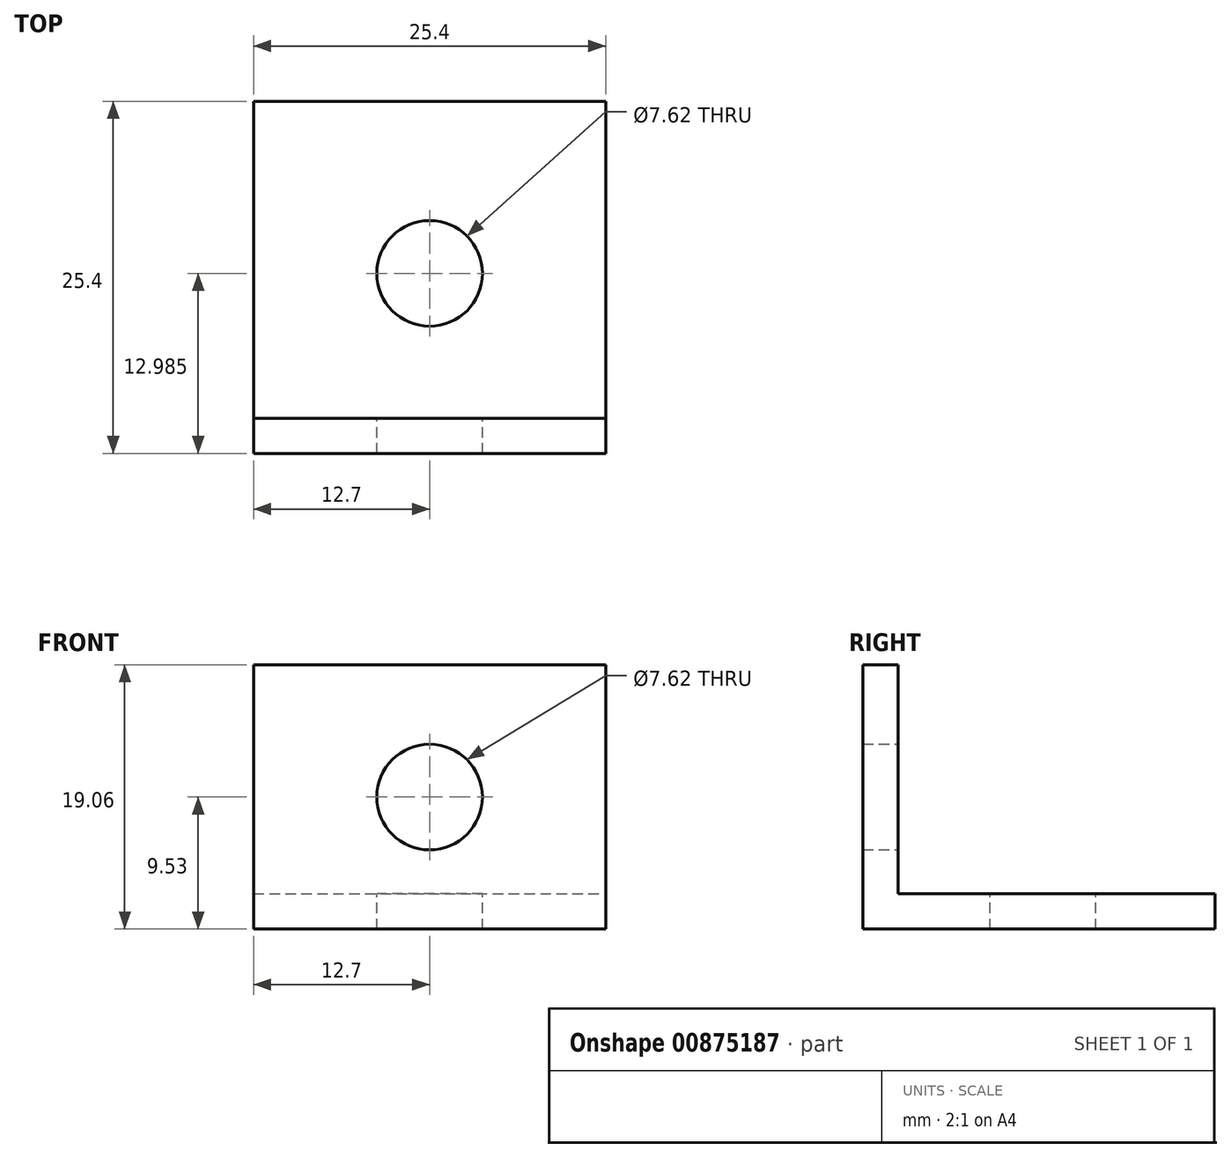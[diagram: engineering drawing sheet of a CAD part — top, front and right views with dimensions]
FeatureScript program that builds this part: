
annotation { "Feature Type Name" : "Feature", "Feature Type Description" : "" }
export const myFeature = defineFeature(function(context is Context, id is Id, definition is map)
    precondition{}
    {
        {
            var Q0;
            Q0=qCreatedBy(makeId("Front.planeOp"),FACE);
            var sketch = newSketch(context, id + "F0", { "sketchPlane" : qUnion([Q0])});
            skLineSegment(sketch, "E0.bottom", {"start": v(-12.7, 9.53) * mm, "end": v(12.7, 9.53) * mm});
            skLineSegment(sketch, "E0.top", {"start": v(-12.7, -9.52) * mm, "end": v(12.7, -9.52) * mm});
            skLineSegment(sketch, "E0.left", {"start": v(-12.7, 9.53) * mm, "end": v(-12.7, -9.52) * mm});
            skLineSegment(sketch, "E0.right", {"start": v(12.7, 9.53) * mm, "end": v(12.7, -9.52) * mm});
            skPoint(sketch, "E0.middle", {"position": v(0, 0) * mm});
            skSolve(sketch);
        }
        {
            var Q0;
            Q0=makeQuery(id+"F0.imprint","IMPRINT",FACE,{"disambiguationData":[TD([[makeQuery(id+"F0.imprint","IMPRINT",EDGE,{"derivedFrom":sQuery(id+"F0.wireOp",EDGE,"E0.bottom")}),-1.0]])]});
            extrude(context, id + "F1", {"entities" : qUnion([Q0]), "depth" : 25.4 * mm, "offsetDistance" : 25.4 * mm});
        }
        {
            var Q0;
            Q0=makeQuery(id+"F1.opExtrude","SWEPT_FACE",FACE,{"disambiguationData":[OSD([sQuery(id+"F0.wireOp",EDGE,"E0.right")])]});
            var Q1;
            Q1=makeQuery(id+"F1.opExtrude","SWEPT_FACE",FACE,{"disambiguationData":[OSD([sQuery(id+"F0.wireOp",EDGE,"E0.bottom")])]});
            var Q2;
            Q2=makeQuery(id+"F1.opExtrude","CAP_FACE",FACE,{"disambiguationData":[OSD([sQuery(id+"F0.wireOp",EDGE,"E0.bottom"),sQuery(id+"F0.wireOp",EDGE,"E0.top"),sQuery(id+"F0.wireOp",EDGE,"E0.left"),sQuery(id+"F0.wireOp",EDGE,"E0.right")])],"isStart":true});
            var Q3;
            Q3=makeQuery(id+"F1.opExtrude","SWEPT_FACE",FACE,{"disambiguationData":[OSD([sQuery(id+"F0.wireOp",EDGE,"E0.left")])]});
            shell(context, id + "F2", {"entities" : qUnion([Q0, Q1, Q2, Q3]), "thickness" : 2.54 * mm});
        }
        {
            var Q0;
            Q0=makeQuery(id+"F2.opShell","OFFSET_FACE",FACE,{"disambiguationData":[OSD([sQuery(id+"F0.wireOp",EDGE,"E0.bottom"),sQuery(id+"F0.wireOp",EDGE,"E0.top"),sQuery(id+"F0.wireOp",EDGE,"E0.left"),sQuery(id+"F0.wireOp",EDGE,"E0.right")])]});
            var sketch = newSketch(context, id + "F3", { "sketchPlane" : qUnion([Q0])});
            skCircle(sketch, "E1", {"center": v(0, 0) * mm, "radius": 3.81 * mm});
            skSolve(sketch);
        }
        {
            var Q0;
            Q0=makeQuery(id+"F2.opShell","OFFSET_FACE",FACE,{"disambiguationData":[OSD([sQuery(id+"F0.wireOp",EDGE,"E0.top")])]});
            var sketch = newSketch(context, id + "F4", { "sketchPlane" : qUnion([Q0])});
            skCircle(sketch, "E2", {"center": v(0, -12.41) * mm, "radius": 3.81 * mm});
            skSolve(sketch);
        }
        {
            var Q0;
            Q0 = qSketchRegion(id + "F3", true);
            extrude(context, id + "F5", {"entities" : qUnion([Q0]), "operationType" : NewBodyOperationType.REMOVE, "oppositeDirection" : true, "depth" : 25.4 * mm, "offsetDistance" : 25.4 * mm});
        }
        {
            var Q0;
            Q0 = qSketchRegion(id + "F4", true);
            extrude(context, id + "F6", {"entities" : qUnion([Q0]), "operationType" : NewBodyOperationType.REMOVE, "oppositeDirection" : true, "depth" : 25.4 * mm, "offsetDistance" : 25.4 * mm});
        }
    });
